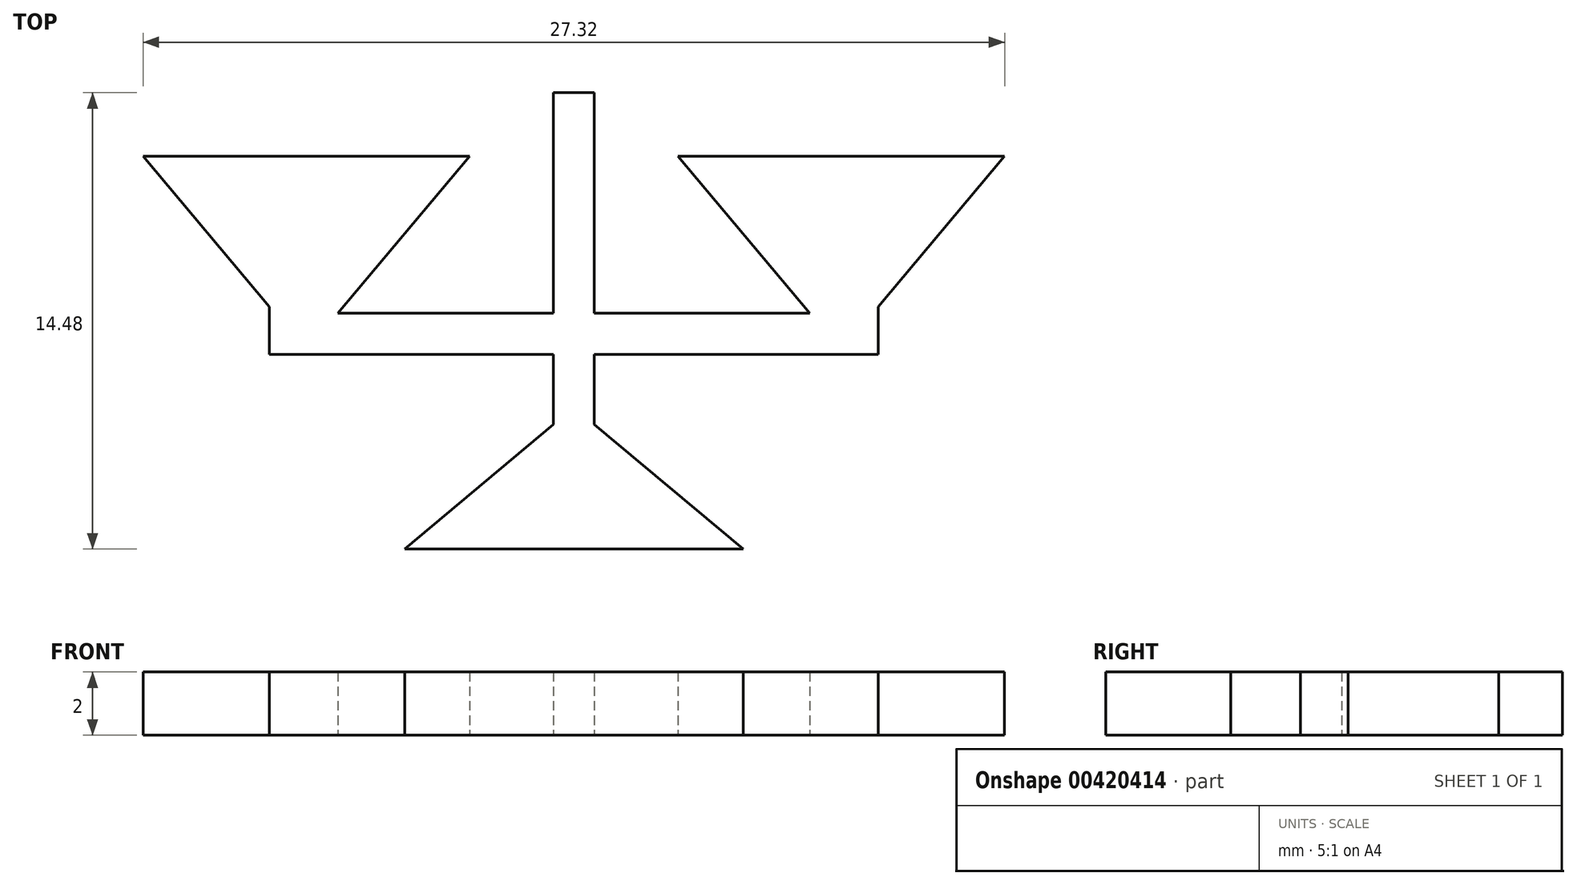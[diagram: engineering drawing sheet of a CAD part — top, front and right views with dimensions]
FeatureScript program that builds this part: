
annotation { "Feature Type Name" : "Feature", "Feature Type Description" : "" }
export const myFeature = defineFeature(function(context is Context, id is Id, definition is map)
    precondition{}
    {
        {
            var Q0;
            Q0=qCreatedBy(makeId("Top.planeOp"),FACE);
            var sketch = newSketch(context, id + "F0", { "sketchPlane" : qUnion([Q0])});
            skLineSegment(sketch, "E0", {"start": v(0, -11.75) * mm, "end": v(0, 20.53) * mm, "construction": true});
            skLineSegment(sketch, "E1", {"start": v(0, 7) * mm, "end": v(0.8, 7) * mm});
            skLineSegment(sketch, "E2", {"start": v(0.8, 7) * mm, "end": v(0.8, 0) * mm});
            skLineSegment(sketch, "E3", {"start": v(0.8, 0) * mm, "end": v(7.16, 0) * mm});
            skLineSegment(sketch, "E4", {"start": v(7.16, 0) * mm, "end": v(2.98, 4.98) * mm});
            skLineSegment(sketch, "E5", {"start": v(2.98, 4.98) * mm, "end": v(13.98, 4.98) * mm});
            skLineSegment(sketch, "E6", {"start": v(13.98, 4.98) * mm, "end": v(9.8, 0) * mm});
            skLineSegment(sketch, "E7", {"start": v(9.8, 0) * mm, "end": v(9.8, -1.6) * mm});
            skLineSegment(sketch, "E8", {"start": v(9.8, -1.6) * mm, "end": v(0.8, -1.6) * mm});
            skLineSegment(sketch, "E9", {"start": v(0.8, -1.6) * mm, "end": v(0.8, -3.6) * mm});
            skLineSegment(sketch, "E10", {"start": v(0.8, -3.6) * mm, "end": v(5.78, -7.78) * mm});
            skLineSegment(sketch, "E11", {"start": v(5.78, -7.78) * mm, "end": v(0, -7.78) * mm});
            skLineSegment(sketch, "E12", {"start": v(8.48, 4.98) * mm, "end": v(8.48, 0) * mm, "construction": true});
            skLineSegment(sketch, "E13.MirrorCS", {"start": v(0, 7) * mm, "end": v(-0.8, 7) * mm});
            skLineSegment(sketch, "E14.MirrorCS", {"start": v(-9.8, 0) * mm, "end": v(-9.8, -1.6) * mm});
            skLineSegment(sketch, "E15.MirrorCS", {"start": v(-0.8, 7) * mm, "end": v(-0.8, 0) * mm});
            skLineSegment(sketch, "E16.MirrorCS", {"start": v(-0.8, 0) * mm, "end": v(-7.16, 0) * mm});
            skLineSegment(sketch, "E17.MirrorCS", {"start": v(-7.16, 0) * mm, "end": v(-2.98, 4.98) * mm});
            skLineSegment(sketch, "E18.MirrorCS", {"start": v(-2.98, 4.98) * mm, "end": v(-13.98, 4.98) * mm});
            skLineSegment(sketch, "E19.MirrorCS", {"start": v(-13.98, 4.98) * mm, "end": v(-9.8, 0) * mm});
            skLineSegment(sketch, "E20.MirrorCS", {"start": v(-9.8, -1.6) * mm, "end": v(-0.8, -1.6) * mm});
            skLineSegment(sketch, "E21.MirrorCS", {"start": v(-0.8, -1.6) * mm, "end": v(-0.8, -3.6) * mm});
            skLineSegment(sketch, "E22.MirrorCS", {"start": v(-0.8, -3.6) * mm, "end": v(-5.78, -7.78) * mm});
            skLineSegment(sketch, "E23.MirrorCS", {"start": v(-5.78, -7.78) * mm, "end": v(0, -7.78) * mm});
            skLineSegment(sketch, "E24.0", {"start": v(-9.65, -1.45) * mm, "end": v(-0.65, -1.45) * mm});
            skLineSegment(sketch, "E24.1", {"start": v(-9.65, 0.05) * mm, "end": v(-9.65, -1.45) * mm});
            skLineSegment(sketch, "E24.2", {"start": v(-13.66, 4.83) * mm, "end": v(-9.65, 0.05) * mm});
            skLineSegment(sketch, "E24.3", {"start": v(-3.3, 4.83) * mm, "end": v(-13.66, 4.83) * mm});
            skLineSegment(sketch, "E24.4", {"start": v(-7.48, -0.15) * mm, "end": v(-3.3, 4.83) * mm});
            skLineSegment(sketch, "E24.5", {"start": v(-0.65, -1.45) * mm, "end": v(-0.65, -3.67) * mm});
            skLineSegment(sketch, "E24.6", {"start": v(-0.65, -0.15) * mm, "end": v(-7.48, -0.15) * mm});
            skLineSegment(sketch, "E24.7", {"start": v(-0.65, 6.85) * mm, "end": v(-0.65, -0.15) * mm});
            skLineSegment(sketch, "E24.8", {"start": v(0, 6.85) * mm, "end": v(-0.65, 6.85) * mm});
            skLineSegment(sketch, "E24.9", {"start": v(0, 6.85) * mm, "end": v(0.65, 6.85) * mm});
            skLineSegment(sketch, "E24.10", {"start": v(0.65, 6.85) * mm, "end": v(0.65, -0.15) * mm});
            skLineSegment(sketch, "E24.11", {"start": v(0.65, -0.15) * mm, "end": v(7.48, -0.15) * mm});
            skLineSegment(sketch, "E24.12", {"start": v(0.65, -3.67) * mm, "end": v(5.37, -7.63) * mm});
            skLineSegment(sketch, "E24.13", {"start": v(5.37, -7.63) * mm, "end": v(0, -7.63) * mm});
            skLineSegment(sketch, "E24.14", {"start": v(-5.37, -7.63) * mm, "end": v(0, -7.63) * mm});
            skLineSegment(sketch, "E24.15", {"start": v(-0.65, -3.67) * mm, "end": v(-5.37, -7.63) * mm});
            skLineSegment(sketch, "E24.16", {"start": v(0.65, -1.45) * mm, "end": v(0.65, -3.67) * mm});
            skLineSegment(sketch, "E24.17", {"start": v(9.65, -1.45) * mm, "end": v(0.65, -1.45) * mm});
            skLineSegment(sketch, "E24.18", {"start": v(9.65, 0.05) * mm, "end": v(9.65, -1.45) * mm});
            skLineSegment(sketch, "E24.19", {"start": v(13.66, 4.83) * mm, "end": v(9.65, 0.05) * mm});
            skLineSegment(sketch, "E24.20", {"start": v(3.3, 4.83) * mm, "end": v(13.66, 4.83) * mm});
            skLineSegment(sketch, "E24.21", {"start": v(7.48, -0.15) * mm, "end": v(3.3, 4.83) * mm});
            skSolve(sketch);
        }
        {
            var Q0;
            Q0=makeQuery(id+"F0.imprint","IMPRINT",FACE,{"disambiguationData":[TD([[makeQuery(id+"F0.imprint","IMPRINT",EDGE,{"derivedFrom":sQuery(id+"F0.wireOp",EDGE,"E24.0")}),1.0]])]});
            extrude(context, id + "F1", {"entities" : qUnion([Q0]), "depth" : 2 * mm});
        }
    });
